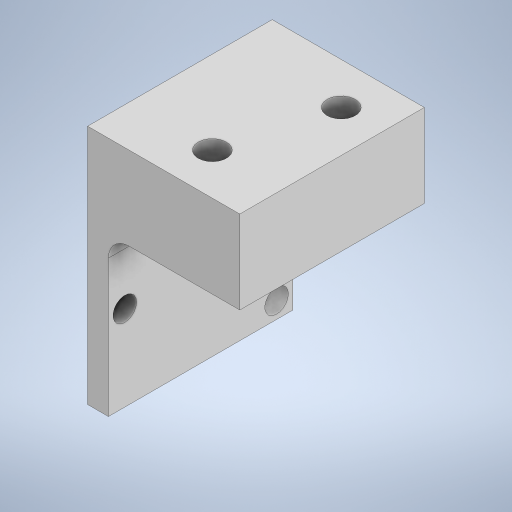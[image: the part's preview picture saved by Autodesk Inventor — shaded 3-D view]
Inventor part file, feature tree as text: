
AUTODESK INVENTOR PART (.ipt)
format: ipt  version: 2024.2 (Build 282272000, 272)  size: 574,976 bytes
history: native  units: in
note: dims shown in document units (in); Inventor stores cm internally (conversion verified against a paired STEP export)
features: extrude x3, sketch x3, fillet x1, chamfer x1, projected_geometry x1
ambient origin geometry x8: Origin, YZ Plane, XZ Plane, XY Plane, X Axis, Y Axis, Z Axis, Center Point
bodies: Solid1 (feature_tree)
feature tree (9):
  extrude  "Extrusion1"  Depth=0.125in
  extrude  "Extrusion2"  Depth=1.11in TaperAngle=0.0deg
  fillet  "Fillet1"  Radius=0.1417in
  extrude  "Extrusion3"  Depth=0.125in
  chamfer  "Chamfer1"  Distance=0.0984in
  sketch  "Sketch1"  dims[d0=0.5in d1=0.125in]
  sketch  "Sketch2"  dims[d2=1.45in d3=1.11in d4=0.0in d5=0.1417in]
  sketch  "Sketch3"  dims[d6=0.1417in d7=0.0984in d8=0.0984in d9=0.0984in d10=0.5118in d11=1.11in d12=0.0in d13=0.125in d14=0.17in d15=0.17in d16=0.25in d18=0.25in d19=0.25in d20=0.25in d21=1.11in d22=0.0in d23=0.125in d24=0.125in d25=45.0deg]
  projected_geometry  "Projected Loop1"
